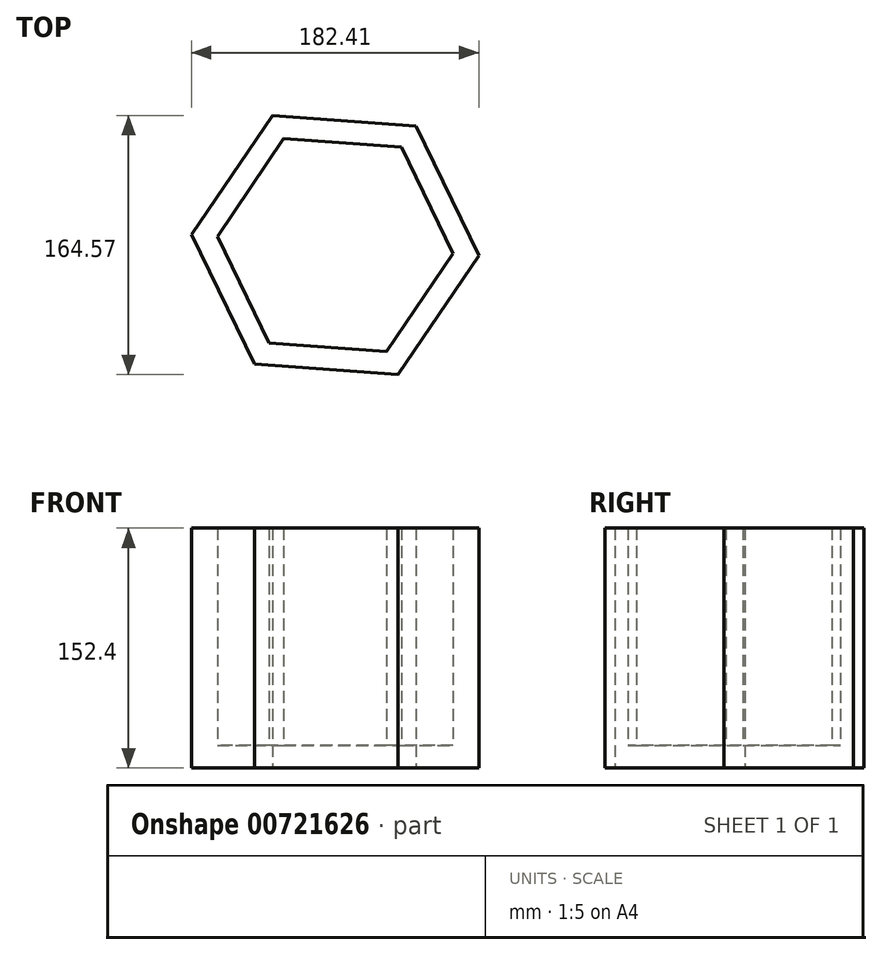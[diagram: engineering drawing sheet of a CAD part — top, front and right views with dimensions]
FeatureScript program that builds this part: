
annotation { "Feature Type Name" : "Feature", "Feature Type Description" : "" }
export const myFeature = defineFeature(function(context is Context, id is Id, definition is map)
    precondition{}
    {
        {
            var Q0;
            Q0=qCreatedBy(makeId("Top.planeOp"),FACE);
            var sketch = newSketch(context, id + "F0", { "sketchPlane" : qUnion([Q0])});
            skCircle(sketch, "E0.cCircle", {"center": v(-10.46, -2.32) * mm, "radius": 79.19 * mm, "construction": true});
            skLineSegment(sketch, "E0.0", {"start": v(80.74, -8.92) * mm, "end": v(29.42, -84.6) * mm});
            skLineSegment(sketch, "E0.1", {"start": v(29.42, -84.6) * mm, "end": v(-61.78, -78) * mm});
            skLineSegment(sketch, "E0.2", {"start": v(-61.78, -78) * mm, "end": v(-101.67, 4.29) * mm});
            skLineSegment(sketch, "E0.3", {"start": v(-101.67, 4.29) * mm, "end": v(-50.35, 79.97) * mm});
            skLineSegment(sketch, "E0.4", {"start": v(-50.35, 79.97) * mm, "end": v(40.85, 73.37) * mm});
            skLineSegment(sketch, "E0.5", {"start": v(40.85, 73.37) * mm, "end": v(80.74, -8.92) * mm});
            skPoint(sketch, "E0.0.midPoint", {"position": v(55.08, -46.76) * mm});
            skSolve(sketch);
        }
        {
            var Q0;
            Q0 = qSketchRegion(id + "F0", true);
            extrude(context, id + "F1", {"entities" : qUnion([Q0]), "depth" : 152.4 * mm, "offsetDistance" : 25.4 * mm});
        }
        {
            var Q0;
            Q0=makeQuery(id+"F1.opExtrude","CAP_FACE",FACE,{"disambiguationData":[OSD([sQuery(id+"F0.wireOp",EDGE,"E0.0"),sQuery(id+"F0.wireOp",EDGE,"E0.1"),sQuery(id+"F0.wireOp",EDGE,"E0.2"),sQuery(id+"F0.wireOp",EDGE,"E0.3"),sQuery(id+"F0.wireOp",EDGE,"E0.4"),sQuery(id+"F0.wireOp",EDGE,"E0.5")])],"isStart":false});
            shell(context, id + "F2", {"entities" : qUnion([Q0]), "thickness" : 14.22 * mm});
        }
    });
